# Revit family: Atdec - MonitorMounts_AWMS_RHXB-1
name_source: partatom
category: Specialty Equipment
revit_build: Autodesk Revit 2014 (Build: 20130308_1515(x64)
units: mm (PartAtom-declared; Revit-internal decimal feet)

## types (1)
- AWMS-RHXB
    Arm = ATD - Aluminum Silver
    Assembly Code = E1010800
    Base = ATD - Aluminum Silver
    Bilt-in arm rotation limiter = Yes
    Colour Options = Silver, White, Black
    Cost = 0 $
    Cover = ATD - Aluminum Silver
    Default Elevation = 0 mm  [stored 0 ft]
    Description = Atdec modular spring-assisted dual display single arm desk mount. (Load: 2-7kg/4.5 -15lb per monitor)
    Height Adjustable = Yes
    Landscape to Portrait Rotaiton = Yes
    Manufacturer = Atdec
    Material = Aluminium, composite plastic
    Model = AWMS-RHXB
    Mounting Hole  Pattern = 75 X 75, 100 X 100
    Mounting Options Included = No
    Note = Choose your preferred desk fixing option
    Option = C type desk clamp (AWM-FC)
Heavy duty desk clamp (AWM-FH)
Grommet mount (AC-GC)
    Product Family = Modular mounting solutions
    Rail = ATD - Aluminum Silver
    Spring-Assisted = Yes
    Support Plate = ATD - Aluminum Black
    Supported Weight Range = 2 - 7kg
    URL = www.atdec.com.au
    Upgradable to Support Additional Arm(s) = Yes
    Warranty = 10 Years

note: [stored X ft] marks values corroborated as IEEE doubles in the binary element streams (Revit-internal decimal feet)

## geometry (parser evidence)
native form markers: Sweep x2
no freeform markers — native parametric forms only
